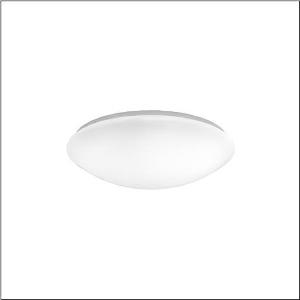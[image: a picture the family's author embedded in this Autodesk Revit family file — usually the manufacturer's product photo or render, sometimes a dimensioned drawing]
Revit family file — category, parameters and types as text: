
# Revit family: round_31_b_5pja132001a
name_source: partatom
category: Lighting Fixtures
units: mm (PartAtom-declared; Revit-internal decimal feet)

## family parameters
Cut with Voids When Loaded = No
Host = Face
Light Source = No
Part Type = Normal
Room Calculation Point = No
Round Connector Dimension = Use Diameter
Shared = No

## types (1)
- Round 31 B (1 x LED, 2500 lm, 19 W, 4000K)
    Apparent Load = 19 VA
    CIE Flux Codes = 42 71 89 88 100
    Color Rendering = 80
    Color Temperature = 4000K
    Default Elevation = 1800 mm
    Description = Round 31 B, wall and ceiling luminaire, primary optical cover: enclosure, of PMMA, light emission: direct distribution, primary light characteristic: symmetric, installation type: surface-mounted, LED, rated luminous flux: 2.500lm, luminous efficacy: 131lm/W, light colour: 840, colour temperature: 4000K, with terminal, 3+2-pole, max. 2.5mm², mains connection: 230V, AC, 50/60Hz, rated input power: 19W, luminaire housing, round, of steel, white, diameter: 360mm, height: 95mm, protection rating (complete): IP40, insulation class (complete): insulation class I (protective earthing), certification: CE, impact resistance: IK02, packaging unit: 1 piece
    Height = 95 mm
    Lamp = 1 x LED
    Lamp Light Flux = 2500 lm
    Lamp Power = 19 W
    Lamp count = 1
    Length = 360 mm
    Luminous efficacy = 132 lm/W
    Manufacturer = Siteco
    ModVariant = No
    Model = 5PJA132001A
    Mounting Place = Ceiling
    Mounting Type = Surface mounted
    Number of Poles = 1
    OnlyDefault = Yes
    Power Factor = 1
    Product Name = Round 31 B
    Product group = wall and ceiling luminaire
    ProductGroupID = 301
    Protection Class = Protection class I
    Protection Degree = IP 40
    RLX_Detail_Level = 1
    RLX_Emergency_Light_Flux = 0 lm
    RLX_Emergency_Type = 0
    RLX_Emergency_Type_DB = No
    RlxData = <blob elided: 10925 chars, md5=de44d33d>
    Socket = socket
    Standby Power = 0 W
    System Light Flux = 2500 lm
    System Power = 19 W
    Type Comments = Product without accessories
    Type Image = l_1258315.jpg
    URL = http://relux.com
    VarID = ---
    Voltage = 0 V
    Weight = 0.00 kg
    Width = 0 mm  [stored 0 ft]

note: [stored X ft] marks values corroborated as IEEE doubles in the binary element streams (Revit-internal decimal feet)

## geometry (parser evidence)
native form markers: Sweep x13
no freeform markers — native parametric forms only
